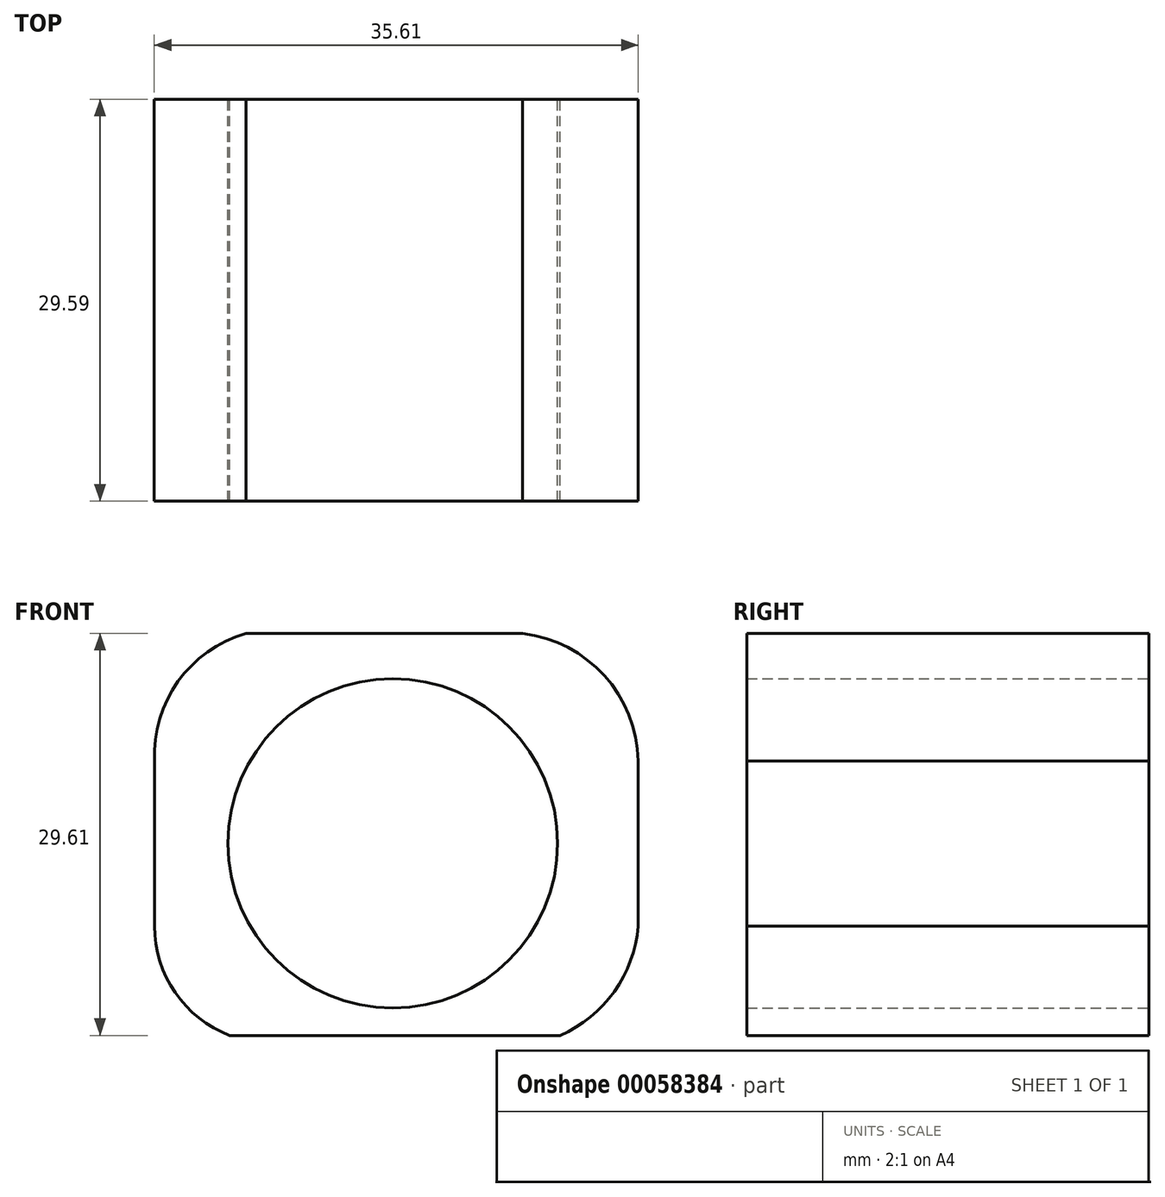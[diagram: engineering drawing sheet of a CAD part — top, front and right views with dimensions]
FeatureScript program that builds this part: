
annotation { "Feature Type Name" : "Feature", "Feature Type Description" : "" }
export const myFeature = defineFeature(function(context is Context, id is Id, definition is map)
    precondition{}
    {
        {
            var Q0;
            Q0=qCreatedBy(makeId("Front.planeOp"),FACE);
            var sketch = newSketch(context, id + "F0", { "sketchPlane" : qUnion([Q0])});
            skLineSegment(sketch, "E0.bottom", {"start": v(0, 0) * mm, "end": v(35.6, 0) * mm});
            skLineSegment(sketch, "E0.top", {"start": v(0, 29.6) * mm, "end": v(35.6, 29.6) * mm});
            skLineSegment(sketch, "E0.left", {"start": v(0, 0) * mm, "end": v(0, 29.6) * mm});
            skLineSegment(sketch, "E0.right", {"start": v(35.6, 0) * mm, "end": v(35.6, 29.6) * mm});
            skArc(sketch, "E1", {"start": v(6.73, 29.6) * mm, "mid": v(1.73, 26.07) * mm, "end": v(0, 20.2) * mm});
            skArc(sketch, "E2", {"start": v(35.6, 20.2) * mm, "mid": v(33.11, 26.5) * mm, "end": v(27.09, 29.6) * mm});
            skArc(sketch, "E3", {"start": v(0, 8.05) * mm, "mid": v(1.52, 3.17) * mm, "end": v(5.54, 0) * mm});
            skArc(sketch, "E4", {"start": v(29.86, 0) * mm, "mid": v(33.84, 3.24) * mm, "end": v(35.6, 8.05) * mm});
            skLineSegment(sketch, "E5", {"start": v(0, 14.8) * mm, "end": v(0, 13.35) * mm});
            skLineSegment(sketch, "E6", {"start": v(35.6, 14.8) * mm, "end": v(35.6, 13.35) * mm});
            skSolve(sketch);
        }
        {
            var Q0;
            Q0=makeQuery(id+"F0.imprint","IMPRINT",FACE,{"disambiguationData":[TD([[makeQuery(id+"F0.imprint","IMPRINT",EDGE,{"derivedFrom":sQuery(id+"F0.wireOp",EDGE,"E0.bottom")}),1.0]])]});
            var sketch = newSketch(context, id + "F1", { "sketchPlane" : qUnion([Q0])});
            skCircle(sketch, "E7", {"center": v(17.54, 14.14) * mm, "radius": 12.13 * mm});
            skSolve(sketch);
        }
        {
            var Q0;
            Q0=qSketchRegion(id+"F0",true);
            extrude(context, id + "F2", {"entities" : qUnion([Q0]), "depth" : 29.59 * mm});
        }
        {
            var Q0;
            Q0=makeQuery(id+"F1.imprint","IMPRINT",FACE,{"disambiguationData":[TD([[makeQuery(id+"F1.imprint","IMPRINT",EDGE,{"derivedFrom":sQuery(id+"F1.wireOp",EDGE,"E7")}),1.0]])]});
            extrude(context, id + "F3", {"entities" : qUnion([Q0]), "operationType" : NewBodyOperationType.REMOVE, "depth" : 40.3 * mm});
        }
        {
            var Q0;
            {var subQ3=sQuery(id+"F0.wireOp",EDGE,"E2");Q0=makeQuery(id+"F0.imprint","IMPRINT",FACE,{"disambiguationData":[TD([[makeQuery(id+"F0.imprint","IMPRINT",EDGE,{"derivedFrom":subQ3}),-1.0]])]});}
            extrude(context, id + "F4", {"entities" : qUnion([Q0]), "operationType" : NewBodyOperationType.REMOVE, "depth" : 51.04 * mm});
        }
        {
            var Q0;
            {var subQ0=sQuery(id+"F0.wireOp",EDGE,"E0.left");var subQ1=sQuery(id+"F0.wireOp",EDGE,"E0.top");var subQ2=makeQuery(id+"F0.imprint","INTERSECT",VERTEX,{"derivedFrom":[subQ1,subQ0]});Q0=makeQuery(id+"F0.imprint","IMPRINT",FACE,{"disambiguationData":[TD([[makeQuery(id+"F0.imprint","IMPRINT",EDGE,{"disambiguationData":[TD([[subQ2,-1.0]])],"derivedFrom":subQ1}),-1.0]])]});}
            extrude(context, id + "F5", {"entities" : qUnion([Q0]), "operationType" : NewBodyOperationType.REMOVE, "depth" : 43.87 * mm});
        }
        {
            var Q0;
            {var subQ3=sQuery(id+"F0.wireOp",EDGE,"E3");Q0=makeQuery(id+"F0.imprint","IMPRINT",FACE,{"disambiguationData":[TD([[makeQuery(id+"F0.imprint","IMPRINT",EDGE,{"derivedFrom":subQ3}),-1.0]])]});}
            extrude(context, id + "F6", {"entities" : qUnion([Q0]), "operationType" : NewBodyOperationType.REMOVE, "depth" : 37.87 * mm});
        }
        {
            var Q0;
            {var subQ3=sQuery(id+"F0.wireOp",EDGE,"E4");Q0=makeQuery(id+"F0.imprint","IMPRINT",FACE,{"disambiguationData":[TD([[makeQuery(id+"F0.imprint","IMPRINT",EDGE,{"derivedFrom":subQ3}),-1.0]])]});}
            extrude(context, id + "F7", {"entities" : qUnion([Q0]), "operationType" : NewBodyOperationType.REMOVE, "depth" : 46.25 * mm});
        }
    });
